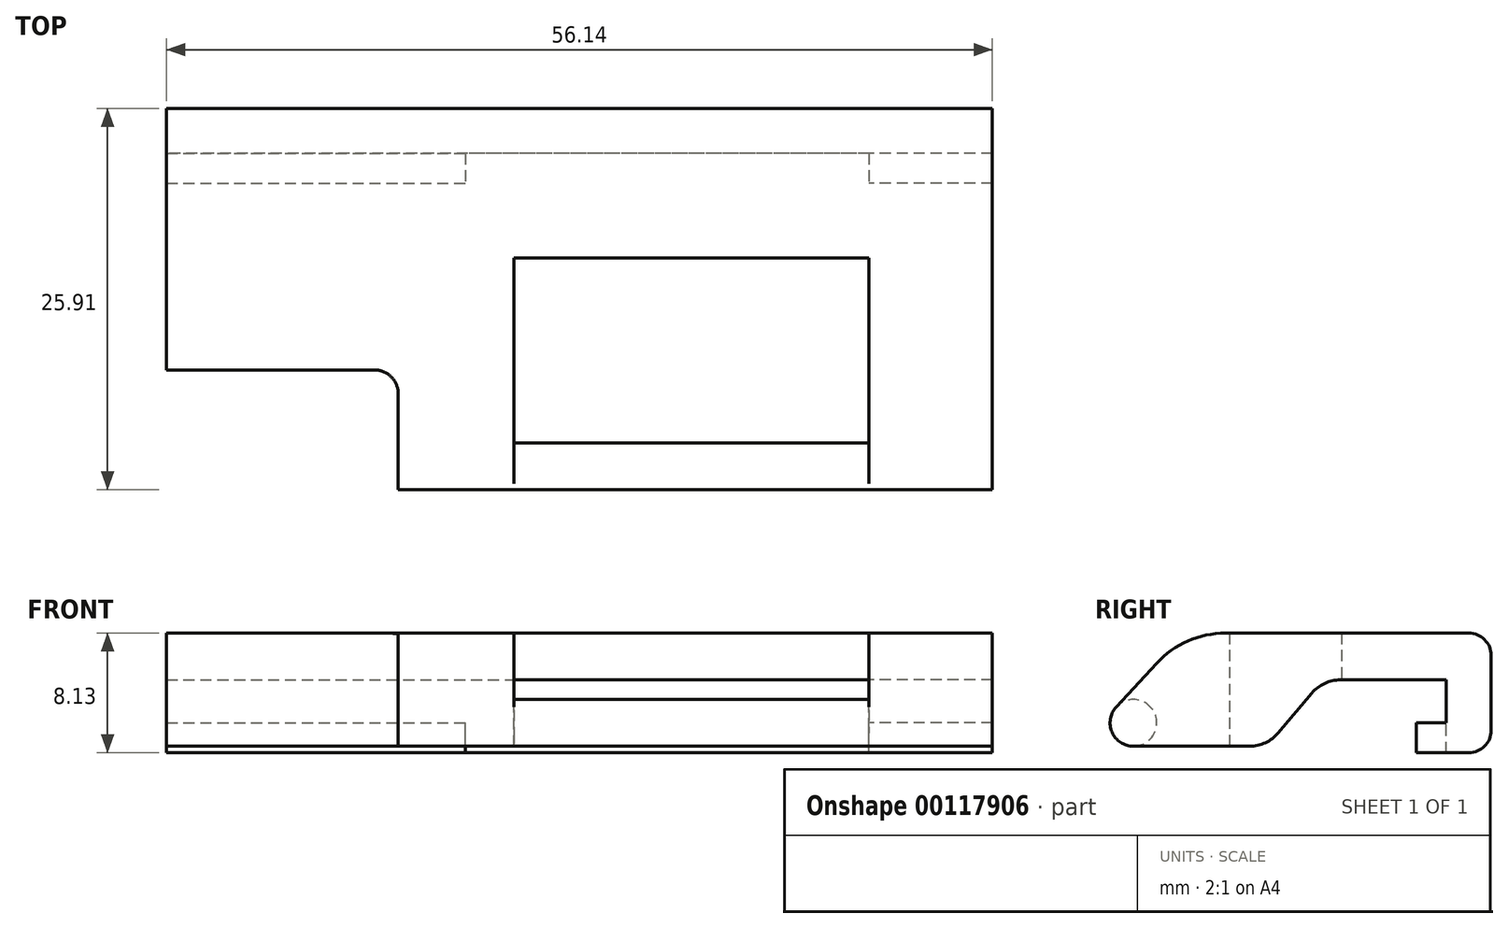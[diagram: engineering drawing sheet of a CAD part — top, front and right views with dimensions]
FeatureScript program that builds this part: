
annotation { "Feature Type Name" : "Feature", "Feature Type Description" : "" }
export const myFeature = defineFeature(function(context is Context, id is Id, definition is map)
    precondition{}
    {
        {
            var Q0;
            Q0=qCreatedBy(makeId("Right.planeOp"),FACE);
            var sketch = newSketch(context, id + "F0", { "sketchPlane" : qUnion([Q0])});
            skCircle(sketch, "E0", {"center": v(0, 0) * mm, "radius": 1.59 * mm});
            skSolve(sketch);
        }
        {
            var Q0;
            Q0 = qSketchRegion(id + "F0", true);
            extrude(context, id + "F1", {"entities" : qUnion([Q0]), "depth" : 12.06 * mm});
        }
        {
            var Q0;
            Q0=makeQuery(id+"F1.opExtrude","CAP_FACE",FACE,{"disambiguationData":[OSD([sQuery(id+"F0.wireOp",EDGE,"E0")])],"isStart":false});
            var sketch = newSketch(context, id + "F2", { "sketchPlane" : qUnion([Q0])});
            skLineSegment(sketch, "E1", {"start": v(24.32, 6.1) * mm, "end": v(24.32, -2.03) * mm});
            skLineSegment(sketch, "E2", {"start": v(24.32, -2.03) * mm, "end": v(19.24, -2.03) * mm});
            skLineSegment(sketch, "E3", {"start": v(19.24, -2.03) * mm, "end": v(19.24, 0) * mm});
            skLineSegment(sketch, "E4", {"start": v(19.24, 0) * mm, "end": v(21.27, 0) * mm});
            skLineSegment(sketch, "E5", {"start": v(21.27, 0) * mm, "end": v(21.27, 2.92) * mm});
            skLineSegment(sketch, "E6", {"start": v(21.27, 2.92) * mm, "end": v(12.9, 2.92) * mm});
            skLineSegment(sketch, "E7", {"start": v(12.9, 2.92) * mm, "end": v(9.08, -1.59) * mm});
            skLineSegment(sketch, "E8", {"start": v(0, -1.59) * mm, "end": v(9.08, -1.59) * mm});
            skLineSegment(sketch, "E9", {"start": v(24.32, 6.1) * mm, "end": v(6.25, 6.1) * mm});
            skLineSegment(sketch, "E10", {"start": v(1.58, 4.05) * mm, "end": v(-1.17, 1.08) * mm});
            skArc(sketch, "E11.0", {"start": v(-1.17, 1.08) * mm, "mid": v(-1.45, -0.64) * mm, "end": v(0, -1.59) * mm});
            skPoint(sketch, "E12.visualSharp", {"position": v(3.47, 6.1) * mm});
            skArc(sketch, "E12.filletArc", {"start": v(6.25, 6.1) * mm, "mid": v(3.7, 5.56) * mm, "end": v(1.58, 4.05) * mm});
            skSolve(sketch);
        }
        {
            var Q0;
            Q0 = qSketchRegion(id + "F2", true);
            extrude(context, id + "F3", {"entities" : qUnion([Q0]), "operationType" : NewBodyOperationType.ADD, "depth" : 8.38 * mm});
        }
        {
            var Q0;
            Q0=makeQuery(id+"F1.opExtrude","SWEPT_BODY",BODY,{"disambiguationData":[OSD([sQuery(id+"F0.wireOp",EDGE,"E0")])]});
            var Q1;
            Q1=qCreatedBy(makeId("Right.planeOp"),FACE);
            mirror(context, id + "F4", {"operationType" : NewBodyOperationType.ADD, "entities" : qUnion([Q0]), "mirrorPlane" : qUnion([Q1])});
        }
        {
            var Q0;
            Q0=makeQuery(id+"F4.opPattern","COPY",FACE,{"derivedFrom":makeQuery(id+"F3.opExtrude","CAP_FACE",FACE,{"disambiguationData":[OSD([sQuery(id+"F2.wireOp",EDGE,"E1"),sQuery(id+"F2.wireOp",EDGE,"E2"),sQuery(id+"F2.wireOp",EDGE,"E3"),sQuery(id+"F2.wireOp",EDGE,"E4"),sQuery(id+"F2.wireOp",EDGE,"E5"),sQuery(id+"F2.wireOp",EDGE,"E6"),sQuery(id+"F2.wireOp",EDGE,"E7"),sQuery(id+"F2.wireOp",EDGE,"E8"),sQuery(id+"F2.wireOp",EDGE,"E9"),sQuery(id+"F2.wireOp",EDGE,"E10"),sQuery(id+"F2.wireOp",EDGE,"E11.0")])],"isStart":true}),"instanceName":"1"});
            var sketch = newSketch(context, id + "F5", { "sketchPlane" : qUnion([Q0])});
            skLineSegment(sketch, "E13.0", {"start": v(24.32, 6.1) * mm, "end": v(14.16, 6.1) * mm});
            skLineSegment(sketch, "E14.0", {"start": v(24.32, 6.1) * mm, "end": v(24.32, -2.03) * mm});
            skLineSegment(sketch, "E14.1", {"start": v(24.32, -2.03) * mm, "end": v(21.27, -2.03) * mm});
            skLineSegment(sketch, "E14.2", {"start": v(21.27, -2.03) * mm, "end": v(21.27, 2.92) * mm});
            skLineSegment(sketch, "E14.3", {"start": v(21.27, 2.92) * mm, "end": v(14.16, 2.92) * mm});
            skPoint(sketch, "E15.orphan", {"position": v(21.27, 0) * mm});
            skPoint(sketch, "E16.orphan", {"position": v(19.24, -2.03) * mm});
            skLineSegment(sketch, "E17", {"start": v(14.16, 6.1) * mm, "end": v(14.16, 2.92) * mm});
            skPoint(sketch, "E18.orphan", {"position": v(12.9, 2.92) * mm});
            skPoint(sketch, "E19.orphan", {"position": v(24.32, 6.1) * mm});
            skSolve(sketch);
        }
        {
            var Q0;
            Q0 = qSketchRegion(id + "F5", true);
            extrude(context, id + "F6", {"entities" : qUnion([Q0]), "operationType" : NewBodyOperationType.ADD, "endBound" : BoundingType.UP_TO_NEXT, "depth" : 25.4 * mm});
        }
        {
            var Q0;
            Q0=makeQuery(id+"F3.opExtrude","SWEPT_EDGE",EDGE,{"disambiguationData":[OSD([sQuery(id+"F2.wireOp",EDGE,"E7"),sQuery(id+"F2.wireOp",EDGE,"E8")])]});
            var Q1;
            Q1=makeQuery(id+"F3.opExtrude","SWEPT_EDGE",EDGE,{"disambiguationData":[OSD([sQuery(id+"F2.wireOp",EDGE,"E6"),sQuery(id+"F2.wireOp",EDGE,"E7")])]});
            var Q2;
            Q2=makeQuery(id+"F4.opPattern","COPY",EDGE,{"derivedFrom":makeQuery(id+"F3.opExtrude","SWEPT_EDGE",EDGE,{"disambiguationData":[OSD([sQuery(id+"F2.wireOp",EDGE,"E7"),sQuery(id+"F2.wireOp",EDGE,"E8")])]}),"instanceName":"1"});
            var Q3;
            Q3=makeQuery(id+"F4.opPattern","COPY",EDGE,{"derivedFrom":makeQuery(id+"F3.opExtrude","SWEPT_EDGE",EDGE,{"disambiguationData":[OSD([sQuery(id+"F2.wireOp",EDGE,"E6"),sQuery(id+"F2.wireOp",EDGE,"E7")])]}),"instanceName":"1"});
            fillet(context, id + "F7", {"entities" : qUnion([Q0, Q1, Q2, Q3]), "radius" : 2.54 * mm, "tangentPropagation" : true, "allowEdgeOverflow" : false});
        }
        {
            var Q0;
            Q0=makeQuery(id+"F4.opPattern","COPY",FACE,{"derivedFrom":makeQuery(id+"F3.opExtrude","CAP_FACE",FACE,{"disambiguationData":[OSD([sQuery(id+"F2.wireOp",EDGE,"E1"),sQuery(id+"F2.wireOp",EDGE,"E2"),sQuery(id+"F2.wireOp",EDGE,"E3"),sQuery(id+"F2.wireOp",EDGE,"E4"),sQuery(id+"F2.wireOp",EDGE,"E5"),sQuery(id+"F2.wireOp",EDGE,"E6"),sQuery(id+"F2.wireOp",EDGE,"E7"),sQuery(id+"F2.wireOp",EDGE,"E8"),sQuery(id+"F2.wireOp",EDGE,"E9"),sQuery(id+"F2.wireOp",EDGE,"E10"),sQuery(id+"F2.wireOp",EDGE,"E11.0"),sQuery(id+"F2.wireOp",EDGE,"E12.filletArc")])],"isStart":false}),"instanceName":"1"});
            var sketch = newSketch(context, id + "F8", { "sketchPlane" : qUnion([Q0])});
            skLineSegment(sketch, "E20.0", {"start": v(-24.32, 6.1) * mm, "end": v(-6.54, 6.1) * mm});
            skLineSegment(sketch, "E20.1", {"start": v(-24.32, 6.1) * mm, "end": v(-24.32, -2.03) * mm});
            skLineSegment(sketch, "E20.2", {"start": v(-24.32, -2.03) * mm, "end": v(-19.24, -2.03) * mm});
            skLineSegment(sketch, "E20.3", {"start": v(-19.24, -2.03) * mm, "end": v(-19.24, 0) * mm});
            skLineSegment(sketch, "E20.4", {"start": v(-19.24, 0) * mm, "end": v(-21.27, 0) * mm});
            skLineSegment(sketch, "E20.5", {"start": v(-21.27, 0) * mm, "end": v(-21.27, 2.92) * mm});
            skLineSegment(sketch, "E20.6", {"start": v(-21.27, 2.92) * mm, "end": v(-14.07, 2.92) * mm});
            skLineSegment(sketch, "E21", {"start": v(-6.54, 6.1) * mm, "end": v(-6.54, -1.59) * mm});
            skPoint(sketch, "E22.orphan", {"position": v(-6.25, 6.1) * mm});
            skPoint(sketch, "E23.orphan", {"position": v(-14.07, 2.92) * mm});
            skArc(sketch, "E24.0", {"start": v(-14.07, 2.92) * mm, "mid": v(-13, 2.68) * mm, "end": v(-12.13, 2.02) * mm});
            skLineSegment(sketch, "E24.1", {"start": v(-12.13, 2.02) * mm, "end": v(-9.84, -0.69) * mm});
            skArc(sketch, "E24.2", {"start": v(-9.84, -0.69) * mm, "mid": v(-8.97, -1.35) * mm, "end": v(-7.9, -1.59) * mm});
            skLineSegment(sketch, "E24.3", {"start": v(-6.54, -1.59) * mm, "end": v(-7.9, -1.59) * mm});
            skPoint(sketch, "E25.orphan", {"position": v(0, -1.59) * mm});
            skSolve(sketch);
        }
        {
            var Q0;
            Q0 = qSketchRegion(id + "F8", true);
            extrude(context, id + "F9", {"entities" : qUnion([Q0]), "operationType" : NewBodyOperationType.ADD, "depth" : 15.24 * mm});
        }
        {
            var Q0;
            Q0=makeQuery(id+"F4.opPattern","COPY",FACE,{"derivedFrom":makeQuery(id+"F3.opExtrude","CAP_FACE",FACE,{"disambiguationData":[OSD([sQuery(id+"F2.wireOp",EDGE,"E1"),sQuery(id+"F2.wireOp",EDGE,"E2"),sQuery(id+"F2.wireOp",EDGE,"E3"),sQuery(id+"F2.wireOp",EDGE,"E4"),sQuery(id+"F2.wireOp",EDGE,"E5"),sQuery(id+"F2.wireOp",EDGE,"E6"),sQuery(id+"F2.wireOp",EDGE,"E7"),sQuery(id+"F2.wireOp",EDGE,"E8"),sQuery(id+"F2.wireOp",EDGE,"E9"),sQuery(id+"F2.wireOp",EDGE,"E10"),sQuery(id+"F2.wireOp",EDGE,"E11.0"),sQuery(id+"F2.wireOp",EDGE,"E12.filletArc")])],"isStart":false}),"instanceName":"1"});
            var sketch = newSketch(context, id + "F10", { "sketchPlane" : qUnion([Q0])});
            skArc(sketch, "E26.0", {"start": v(-6.25, 6.1) * mm, "mid": v(-3.7, 5.56) * mm, "end": v(-1.58, 4.05) * mm});
            skLineSegment(sketch, "E26.1", {"start": v(-6.54, 6.1) * mm, "end": v(-6.54, -1.59) * mm});
            skLineSegment(sketch, "E26.2", {"start": v(0, -1.59) * mm, "end": v(-6.54, -1.59) * mm});
            skArc(sketch, "E26.3", {"start": v(1.17, 1.08) * mm, "mid": v(1.45, -0.64) * mm, "end": v(0, -1.59) * mm});
            skLineSegment(sketch, "E26.4", {"start": v(-1.58, 4.05) * mm, "end": v(1.17, 1.08) * mm});
            skLineSegment(sketch, "E26.5", {"start": v(-6.54, 6.1) * mm, "end": v(-6.25, 6.1) * mm});
            skSolve(sketch);
        }
        {
            var Q0;
            Q0 = qSketchRegion(id + "F10", true);
            extrude(context, id + "F11", {"entities" : qUnion([Q0]), "operationType" : NewBodyOperationType.REMOVE, "oppositeDirection" : true, "depth" : 0.5 * mm});
        }
        {
            var Q0;
            {var subQ0=makeQuery(id+"F3.opExtrude","SWEPT_EDGE",EDGE,{"disambiguationData":[OSD([sQuery(id+"F2.wireOp",EDGE,"E1"),sQuery(id+"F2.wireOp",EDGE,"E9")])]});Q0=makeQuery(id+"F9.boolean.opBoolean","MERGE",EDGE,{"derivedFrom":[makeQuery(id+"F6.boolean.opBoolean","MERGE",EDGE,{"derivedFrom":[subQ0,makeQuery(id+"F4.opPattern","COPY",EDGE,{"derivedFrom":subQ0,"instanceName":"1"}),makeQuery(id+"F6.opExtrude","SWEPT_EDGE",EDGE,{"disambiguationData":[OSD([sQuery(id+"F5.wireOp",EDGE,"E13.0"),sQuery(id+"F5.wireOp",EDGE,"E14.0")])]})]}),makeQuery(id+"F9.opExtrude","SWEPT_EDGE",EDGE,{"disambiguationData":[OSD([sQuery(id+"F8.wireOp",EDGE,"E20.0"),sQuery(id+"F8.wireOp",EDGE,"E20.1")])]})]});}
            var Q1;
            {var subQ0=sQuery(id+"F2.wireOp",EDGE,"E2");var subQ1=sQuery(id+"F2.wireOp",EDGE,"E1");var subQ2=makeQuery(id+"F3.opExtrude","SWEPT_EDGE",EDGE,{"disambiguationData":[OSD([subQ1,subQ0])]});Q1=makeQuery(id+"F9.boolean.opBoolean","MERGE",EDGE,{"derivedFrom":[makeQuery(id+"F6.boolean.opBoolean","MERGE",EDGE,{"derivedFrom":[subQ2,makeQuery(id+"F4.opPattern","COPY",EDGE,{"derivedFrom":subQ2,"instanceName":"1"}),makeQuery(id+"F6.opExtrude","SWEPT_EDGE",EDGE,{"disambiguationData":[OSD([subQ1,subQ0])]})]}),makeQuery(id+"F9.opExtrude","SWEPT_EDGE",EDGE,{"disambiguationData":[OSD([sQuery(id+"F8.wireOp",EDGE,"E20.1"),sQuery(id+"F8.wireOp",EDGE,"E20.2")])]})]});}
            fillet(context, id + "F12", {"entities" : qUnion([Q0, Q1]), "radius" : 1.52 * mm, "tangentPropagation" : true, "allowEdgeOverflow" : false});
        }
        {
            var Q0;
            {var subQ0=sQuery(id+"F2.wireOp",EDGE,"E2");var subQ1=makeQuery(id+"F3.opExtrude","SWEPT_FACE",FACE,{"disambiguationData":[OSD([subQ0])]});var subQ2=sQuery(id+"F2.wireOp",EDGE,"E5");var subQ4=sQuery(id+"F2.wireOp",EDGE,"E3");var subQ5=sQuery(id+"F2.wireOp",EDGE,"E4");Q0=makeQuery(id+"F6.boolean.opBoolean","SPLIT",FACE,{"disambiguationData":[TD([subQ1])],"derivedFrom":makeQuery(id+"F4.opPattern","COPY",FACE,{"derivedFrom":makeQuery(id+"F3.opExtrude","CAP_FACE",FACE,{"disambiguationData":[OSD([sQuery(id+"F2.wireOp",EDGE,"E1"),subQ0,subQ4,subQ5,subQ2,sQuery(id+"F2.wireOp",EDGE,"E6"),sQuery(id+"F2.wireOp",EDGE,"E7"),sQuery(id+"F2.wireOp",EDGE,"E8"),sQuery(id+"F2.wireOp",EDGE,"E9"),sQuery(id+"F2.wireOp",EDGE,"E10"),sQuery(id+"F2.wireOp",EDGE,"E11.0"),sQuery(id+"F2.wireOp",EDGE,"E12.filletArc")])],"isStart":true}),"instanceName":"1"})});}
            var sketch = newSketch(context, id + "F13", { "sketchPlane" : qUnion([Q0])});
            skLineSegment(sketch, "E27.0", {"start": v(21.27, -2.03) * mm, "end": v(19.24, -2.03) * mm});
            skLineSegment(sketch, "E27.1", {"start": v(19.24, -2.03) * mm, "end": v(19.24, 0) * mm});
            skLineSegment(sketch, "E27.2", {"start": v(19.24, 0) * mm, "end": v(21.27, 0) * mm});
            skLineSegment(sketch, "E27.3", {"start": v(21.27, -2.03) * mm, "end": v(21.27, 0) * mm});
            skSolve(sketch);
        }
        {
            var Q0;
            Q0 = qSketchRegion(id + "F13", true);
            extrude(context, id + "F14", {"entities" : qUnion([Q0]), "operationType" : NewBodyOperationType.REMOVE, "oppositeDirection" : true, "depth" : 3.3 * mm});
        }
        {
            var Q0;
            Q0=makeQuery(id+"F11.boolean.opBoolean","COPY",EDGE,{"derivedFrom":makeQuery(id+"F11.opExtrude","CAP_EDGE",EDGE,{"disambiguationData":[OSD([sQuery(id+"F10.wireOp",EDGE,"E26.1")])],"isStart":false})});
            fillet(context, id + "F15", {"entities" : qUnion([Q0]), "radius" : 1.59 * mm, "tangentPropagation" : true, "allowEdgeOverflow" : false});
        }
    });
